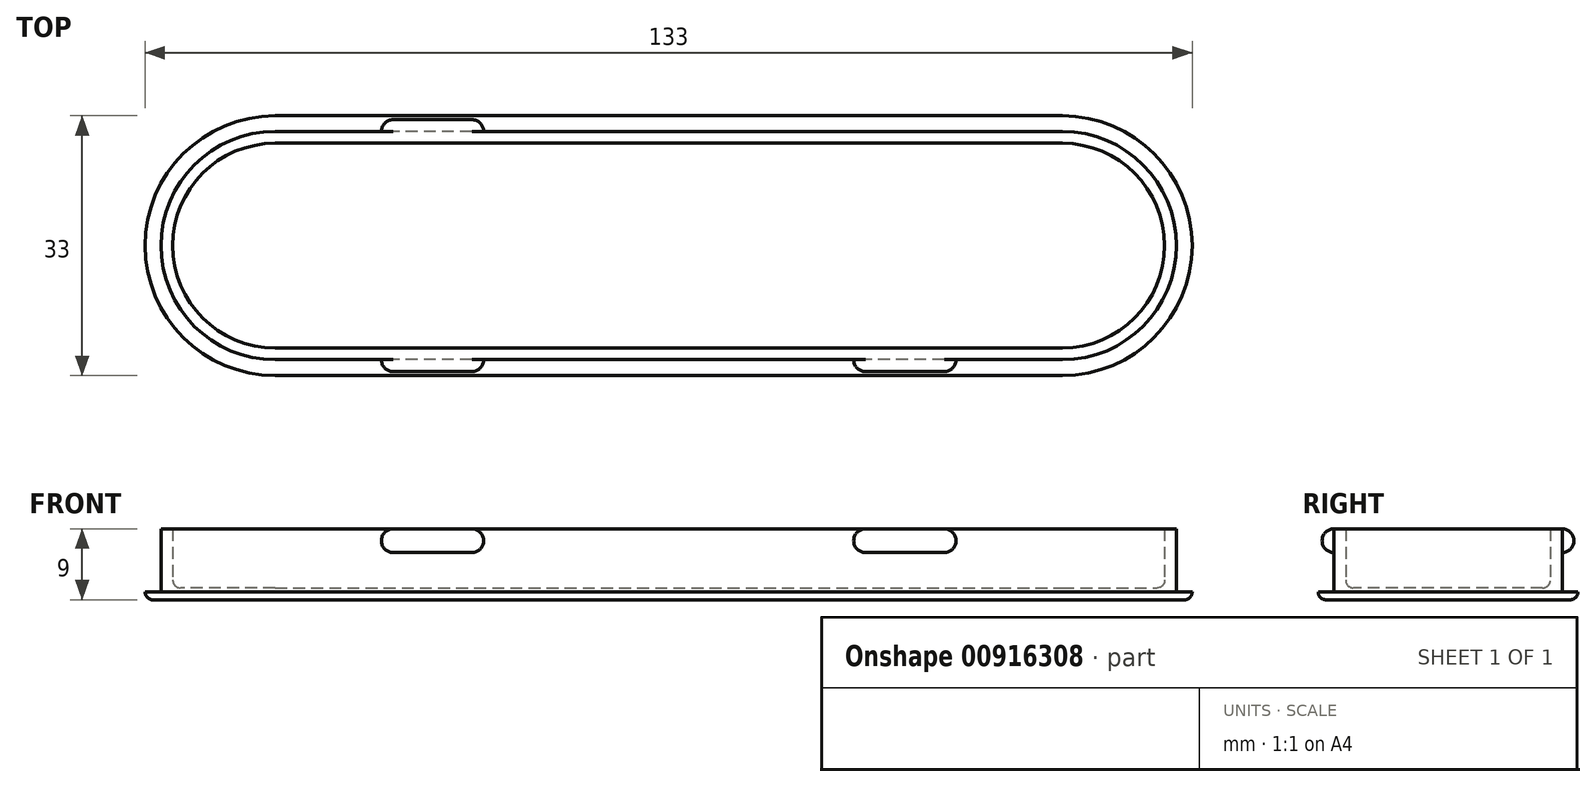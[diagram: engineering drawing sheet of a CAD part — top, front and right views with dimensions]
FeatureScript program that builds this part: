
annotation { "Feature Type Name" : "Feature", "Feature Type Description" : "" }
export const myFeature = defineFeature(function(context is Context, id is Id, definition is map)
    precondition{}
    {
        {
            var Q0;
            Q0=qCreatedBy(makeId("Top.planeOp"),FACE);
            var sketch = newSketch(context, id + "F0", { "sketchPlane" : qUnion([Q0])});
            skLineSegment(sketch, "E0.bottom", {"start": v(50, 14.5) * mm, "end": v(-50, 14.5) * mm});
            skLineSegment(sketch, "E0.top", {"start": v(50, -14.5) * mm, "end": v(-50, -14.5) * mm});
            skLineSegment(sketch, "E0.left", {"start": v(64.5, 0) * mm, "end": v(64.5, 0) * mm});
            skLineSegment(sketch, "E0.right", {"start": v(-64.5, 0) * mm, "end": v(-64.5, 0) * mm});
            skPoint(sketch, "E0.middle", {"position": v(0, 0) * mm});
            skPoint(sketch, "E1.visualSharp", {"position": v(64.5, -14.5) * mm});
            skArc(sketch, "E1.filletArc", {"start": v(50, -14.5) * mm, "mid": v(60.25, -10.25) * mm, "end": v(64.5, 0) * mm});
            skPoint(sketch, "E2.visualSharp", {"position": v(64.5, 14.5) * mm});
            skArc(sketch, "E2.filletArc", {"start": v(64.5, 0) * mm, "mid": v(60.25, 10.25) * mm, "end": v(50, 14.5) * mm});
            skPoint(sketch, "E3.visualSharp", {"position": v(-64.5, -14.5) * mm});
            skArc(sketch, "E3.filletArc", {"start": v(-64.5, 0) * mm, "mid": v(-60.25, -10.25) * mm, "end": v(-50, -14.5) * mm});
            skPoint(sketch, "E4.visualSharp", {"position": v(-64.5, 14.5) * mm});
            skArc(sketch, "E4.filletArc", {"start": v(-50, 14.5) * mm, "mid": v(-60.25, 10.25) * mm, "end": v(-64.5, 0) * mm});
            skArc(sketch, "E5", {"start": v(50, -16.5) * mm, "mid": v(66.5, 0) * mm, "end": v(50, 16.5) * mm});
            skLineSegment(sketch, "E6", {"start": v(50, 16.5) * mm, "end": v(0, 16.5) * mm});
            skLineSegment(sketch, "E7", {"start": v(50, -16.5) * mm, "end": v(0, -16.5) * mm});
            skLineSegment(sketch, "E8.MirrorCS", {"start": v(-50, 16.5) * mm, "end": v(0, 16.5) * mm});
            skArc(sketch, "E9.MirrorCS", {"start": v(-50, -16.5) * mm, "mid": v(-66.5, 0) * mm, "end": v(-50, 16.5) * mm});
            skLineSegment(sketch, "E10.MirrorCS", {"start": v(-50, -16.5) * mm, "end": v(0, -16.5) * mm});
            skSolve(sketch);
        }
        {
            var Q0;
            Q0=makeQuery(id+"F0.imprint","IMPRINT",FACE,{"disambiguationData":[TD([[makeQuery(id+"F0.imprint","IMPRINT",EDGE,{"derivedFrom":sQuery(id+"F0.wireOp",EDGE,"E0.bottom")}),1.0]])]});
            extrude(context, id + "F1", {"entities" : qUnion([Q0]), "depth" : 6 * mm, "offsetDistance" : 25 * mm});
        }
        {
            var Q0;
            Q0=makeQuery(id+"F0.imprint","IMPRINT",FACE,{"disambiguationData":[TD([[makeQuery(id+"F0.imprint","IMPRINT",EDGE,{"derivedFrom":sQuery(id+"F0.wireOp",EDGE,"E0.bottom")}),-1.0]])]});
            extrude(context, id + "F2", {"entities" : qUnion([Q0]), "operationType" : NewBodyOperationType.ADD, "depth" : 1 * mm, "offsetDistance" : 25 * mm});
        }
        {
            var Q0;
            Q0=makeQuery(id+"F1.opExtrude","CAP_FACE",FACE,{"disambiguationData":[OSD([sQuery(id+"F0.wireOp",EDGE,"E0.bottom"),sQuery(id+"F0.wireOp",EDGE,"E0.top"),sQuery(id+"F0.wireOp",EDGE,"E1.filletArc"),sQuery(id+"F0.wireOp",EDGE,"E2.filletArc"),sQuery(id+"F0.wireOp",EDGE,"E3.filletArc"),sQuery(id+"F0.wireOp",EDGE,"E4.filletArc")])],"isStart":false});
            var sketch = newSketch(context, id + "F3", { "sketchPlane" : qUnion([Q0])});
            skLineSegment(sketch, "E11", {"start": v(-35, 14.5) * mm, "end": v(-35, 16) * mm});
            skLineSegment(sketch, "E12", {"start": v(-35, 16) * mm, "end": v(-25, 16) * mm});
            skLineSegment(sketch, "E13", {"start": v(-25, 16) * mm, "end": v(-25, 14.5) * mm});
            skArc(sketch, "E14", {"start": v(-25, 16) * mm, "mid": v(-23.94, 15.56) * mm, "end": v(-23.5, 14.5) * mm});
            skArc(sketch, "E15", {"start": v(-35, 16) * mm, "mid": v(-36.06, 15.56) * mm, "end": v(-36.5, 14.5) * mm});
            skArc(sketch, "E16.MirrorCS", {"start": v(35, 16) * mm, "mid": v(36.06, 15.56) * mm, "end": v(36.5, 14.5) * mm});
            skLineSegment(sketch, "E17.MirrorCS", {"start": v(35, 16) * mm, "end": v(25, 16) * mm});
            skArc(sketch, "E18.MirrorCS", {"start": v(25, 16) * mm, "mid": v(23.94, 15.56) * mm, "end": v(23.5, 14.5) * mm});
            skLineSegment(sketch, "E19.MirrorCS", {"start": v(-35, -16) * mm, "end": v(-25, -16) * mm});
            skArc(sketch, "E20.MirrorCS", {"start": v(-35, -16) * mm, "mid": v(-36.06, -15.56) * mm, "end": v(-36.5, -14.5) * mm});
            skArc(sketch, "E21.MirrorCS", {"start": v(-25, -16) * mm, "mid": v(-23.94, -15.56) * mm, "end": v(-23.5, -14.5) * mm});
            skLineSegment(sketch, "E22.MirrorCS", {"start": v(35, -16) * mm, "end": v(25, -16) * mm});
            skArc(sketch, "E23.MirrorCS", {"start": v(25, -16) * mm, "mid": v(23.94, -15.56) * mm, "end": v(23.5, -14.5) * mm});
            skArc(sketch, "E24.MirrorCS", {"start": v(35, -16) * mm, "mid": v(36.06, -15.56) * mm, "end": v(36.5, -14.5) * mm});
            skSolve(sketch);
        }
        {
            var Q0;
            {var subQ0=makeQuery(id+"F1.opExtrude","CAP_EDGE",EDGE,{"disambiguationData":[OSD([sQuery(id+"F0.wireOp",EDGE,"E1.filletArc"),sQuery(id+"F0.wireOp",EDGE,"E2.filletArc")])],"isStart":false});Q0=makeQuery(id+"F3.imprint","IMPRINT",FACE,{"disambiguationData":[TD([[makeQuery(id+"F3.imprint","IMPRINT",EDGE,{"derivedFrom":subQ0}),1.0]])]});}
            var Q1;
            {var subQ0=sQuery(id+"F3.wireOp",EDGE,"E11");Q1=makeQuery(id+"F3.imprint","IMPRINT",FACE,{"disambiguationData":[TD([[makeQuery(id+"F3.imprint","IMPRINT",EDGE,{"derivedFrom":subQ0}),-1.0]])]});}
            var Q2;
            {var subQ0=sQuery(id+"F3.wireOp",EDGE,"E11");Q2=makeQuery(id+"F3.imprint","IMPRINT",FACE,{"disambiguationData":[TD([[makeQuery(id+"F3.imprint","IMPRINT",EDGE,{"derivedFrom":subQ0}),1.0]])]});}
            var Q3;
            {var subQ0=sQuery(id+"F3.wireOp",EDGE,"E13");Q3=makeQuery(id+"F3.imprint","IMPRINT",FACE,{"disambiguationData":[TD([[makeQuery(id+"F3.imprint","IMPRINT",EDGE,{"derivedFrom":subQ0}),1.0]])]});}
            var Q4;
            Q4=makeQuery(id+"F3.imprint","IMPRINT",FACE,{"disambiguationData":[TD([[makeQuery(id+"F3.imprint","IMPRINT",EDGE,{"derivedFrom":sQuery(id+"F3.wireOp",EDGE,"E19.MirrorCS")}),1.0]])]});
            var Q5;
            {var subQ0=sQuery(id+"F3.wireOp",EDGE,"E16.MirrorCS");Q5=makeQuery(id+"F3.imprint","IMPRINT",FACE,{"disambiguationData":[TD([[makeQuery(id+"F3.imprint","IMPRINT",EDGE,{"derivedFrom":subQ0}),-1.0]])]});}
            var Q6;
            Q6=makeQuery(id+"F3.imprint","IMPRINT",FACE,{"disambiguationData":[TD([[makeQuery(id+"F3.imprint","IMPRINT",EDGE,{"derivedFrom":sQuery(id+"F3.wireOp",EDGE,"E22.MirrorCS")}),-1.0]])]});
            extrude(context, id + "F4", {"entities" : qUnion([Q0, Q1, Q2, Q3, Q4, Q5, Q6]), "operationType" : NewBodyOperationType.ADD, "depth" : 3 * mm, "offsetDistance" : 25 * mm});
        }
        {
            var Q0;
            Q0=makeQuery(id+"F4.opExtrude","CAP_EDGE",EDGE,{"disambiguationData":[OSD([sQuery(id+"F3.wireOp",EDGE,"E19.MirrorCS")])],"isStart":false});
            var Q1;
            Q1=makeQuery(id+"F4.opExtrude","CAP_EDGE",EDGE,{"disambiguationData":[OSD([sQuery(id+"F3.wireOp",EDGE,"E19.MirrorCS")])],"isStart":true});
            var Q2;
            Q2=makeQuery(id+"F4.opExtrude","CAP_EDGE",EDGE,{"disambiguationData":[OSD([sQuery(id+"F3.wireOp",EDGE,"E12")])],"isStart":true});
            var Q3;
            Q3=makeQuery(id+"F4.opExtrude","CAP_EDGE",EDGE,{"disambiguationData":[OSD([sQuery(id+"F3.wireOp",EDGE,"E12")])],"isStart":false});
            var Q4;
            Q4=makeQuery(id+"F4.opExtrude","CAP_EDGE",EDGE,{"disambiguationData":[OSD([sQuery(id+"F3.wireOp",EDGE,"E17.MirrorCS")])],"isStart":false});
            var Q5;
            Q5=makeQuery(id+"F4.opExtrude","CAP_EDGE",EDGE,{"disambiguationData":[OSD([sQuery(id+"F3.wireOp",EDGE,"E17.MirrorCS")])],"isStart":true});
            var Q6;
            Q6=makeQuery(id+"F4.opExtrude","CAP_EDGE",EDGE,{"disambiguationData":[OSD([sQuery(id+"F3.wireOp",EDGE,"E22.MirrorCS")])],"isStart":false});
            var Q7;
            Q7=makeQuery(id+"F4.opExtrude","CAP_EDGE",EDGE,{"disambiguationData":[OSD([sQuery(id+"F3.wireOp",EDGE,"E22.MirrorCS")])],"isStart":true});
            fillet(context, id + "F5", {"entities" : qUnion([Q0, Q1, Q2, Q3, Q4, Q5, Q6, Q7]), "tangentPropagation" : true, "radius" : 1.5 * mm, "defaultsChanged" : false, "vertexSettings" : [], "allowEdgeOverflow" : false});
        }
        {
            var Q0;
            Q0=makeQuery(id+"F4.opExtrude","CAP_FACE",FACE,{"disambiguationData":[OSD([sQuery(id+"F0.wireOp",EDGE,"E0.bottom"),sQuery(id+"F0.wireOp",EDGE,"E0.top"),sQuery(id+"F0.wireOp",EDGE,"E1.filletArc"),sQuery(id+"F0.wireOp",EDGE,"E2.filletArc"),sQuery(id+"F0.wireOp",EDGE,"E3.filletArc"),sQuery(id+"F0.wireOp",EDGE,"E4.filletArc"),sQuery(id+"F3.wireOp",EDGE,"E12"),sQuery(id+"F3.wireOp",EDGE,"E14"),sQuery(id+"F3.wireOp",EDGE,"E15"),sQuery(id+"F3.wireOp",EDGE,"E16.MirrorCS"),sQuery(id+"F3.wireOp",EDGE,"E17.MirrorCS"),sQuery(id+"F3.wireOp",EDGE,"E18.MirrorCS"),sQuery(id+"F3.wireOp",EDGE,"E19.MirrorCS"),sQuery(id+"F3.wireOp",EDGE,"E20.MirrorCS"),sQuery(id+"F3.wireOp",EDGE,"E21.MirrorCS"),sQuery(id+"F3.wireOp",EDGE,"E22.MirrorCS"),sQuery(id+"F3.wireOp",EDGE,"E23.MirrorCS"),sQuery(id+"F3.wireOp",EDGE,"E24.MirrorCS")])],"isStart":false});
            shell(context, id + "F6", {"entities" : qUnion([Q0]), "thickness" : 1.5 * mm});
        }
        {
            var Q0;
            Q0=makeQuery(id+"F2.opExtrude","CAP_EDGE",EDGE,{"disambiguationData":[OSD([sQuery(id+"F0.wireOp",EDGE,"E1.filletArc"),sQuery(id+"F0.wireOp",EDGE,"E2.filletArc")])],"isStart":false});
            var Q1;
            Q1=makeQuery(id+"F2.opExtrude","CAP_EDGE",EDGE,{"disambiguationData":[OSD([sQuery(id+"F0.wireOp",EDGE,"E6"),sQuery(id+"F0.wireOp",EDGE,"E8.MirrorCS")])],"isStart":true});
            var Q2;
            {var subQ0=sQuery(id+"F0.wireOp",EDGE,"E0.top");var subQ1=makeQuery(id+"F1.opExtrude","CAP_EDGE",EDGE,{"disambiguationData":[OSD([subQ0])],"isStart":false});var subQ2=sQuery(id+"F0.wireOp",EDGE,"E4.filletArc");var subQ3=sQuery(id+"F0.wireOp",EDGE,"E3.filletArc");var subQ4=sQuery(id+"F0.wireOp",EDGE,"E2.filletArc");var subQ5=sQuery(id+"F0.wireOp",EDGE,"E1.filletArc");var subQ6=sQuery(id+"F0.wireOp",EDGE,"E0.bottom");Q2=makeQuery(id+"F6.opShell","TWEAK_EDGE",EDGE,{"derivedFrom":[makeQuery(id+"F2.boolean.opBoolean","MERGE",FACE,{"derivedFrom":[makeQuery(id+"F1.opExtrude","CAP_FACE",FACE,{"disambiguationData":[OSD([subQ6,subQ0,subQ5,subQ4,subQ3,subQ2])],"isStart":true}),makeQuery(id+"F2.opExtrude","CAP_FACE",FACE,{"disambiguationData":[OSD([subQ6,subQ0,subQ5,subQ4,subQ3,subQ2,sQuery(id+"F0.wireOp",EDGE,"E5"),sQuery(id+"F0.wireOp",EDGE,"E6"),sQuery(id+"F0.wireOp",EDGE,"E7"),sQuery(id+"F0.wireOp",EDGE,"E8.MirrorCS"),sQuery(id+"F0.wireOp",EDGE,"E9.MirrorCS"),sQuery(id+"F0.wireOp",EDGE,"E10.MirrorCS")])],"isStart":true})]}),makeQuery(id+"F4.boolean.opBoolean","MERGE",FACE,{"derivedFrom":[makeQuery(id+"F1.opExtrude","SWEPT_FACE",FACE,{"disambiguationData":[OSD([subQ0])]}),makeQuery(id+"F4.opExtrude","SWEPT_FACE",FACE,{"disambiguationData":[OSD([subQ0]),TDD([makeQuery(id+"F3.imprint","IMPRINT",EDGE,{"disambiguationData":[TD([[makeQuery(id+"F3.imprint","INTERSECT",VERTEX,{"derivedFrom":[subQ1,sQuery(id+"F3.wireOp",EDGE,"E24.MirrorCS")]}),1.0]])],"derivedFrom":subQ1})])]}),makeQuery(id+"F4.opExtrude","SWEPT_FACE",FACE,{"disambiguationData":[OSD([subQ0]),TDD([makeQuery(id+"F3.imprint","IMPRINT",EDGE,{"disambiguationData":[TD([[makeQuery(id+"F3.imprint","INTERSECT",VERTEX,{"derivedFrom":[subQ1,sQuery(id+"F3.wireOp",EDGE,"E20.MirrorCS")]}),-1.0]])],"derivedFrom":subQ1})])]}),makeQuery(id+"F4.opExtrude","SWEPT_FACE",FACE,{"disambiguationData":[OSD([subQ0]),TDD([makeQuery(id+"F3.imprint","IMPRINT",EDGE,{"disambiguationData":[TD([[makeQuery(id+"F3.imprint","INTERSECT",VERTEX,{"derivedFrom":[subQ1,sQuery(id+"F3.wireOp",EDGE,"E21.MirrorCS")]}),1.0]])],"derivedFrom":subQ1})])]})]})]});}
            fillet(context, id + "F7", {"entities" : qUnion([Q0, Q1, Q2]), "tangentPropagation" : true, "radius" : 1 * mm, "defaultsChanged" : false, "vertexSettings" : [], "allowEdgeOverflow" : false});
        }
    });
